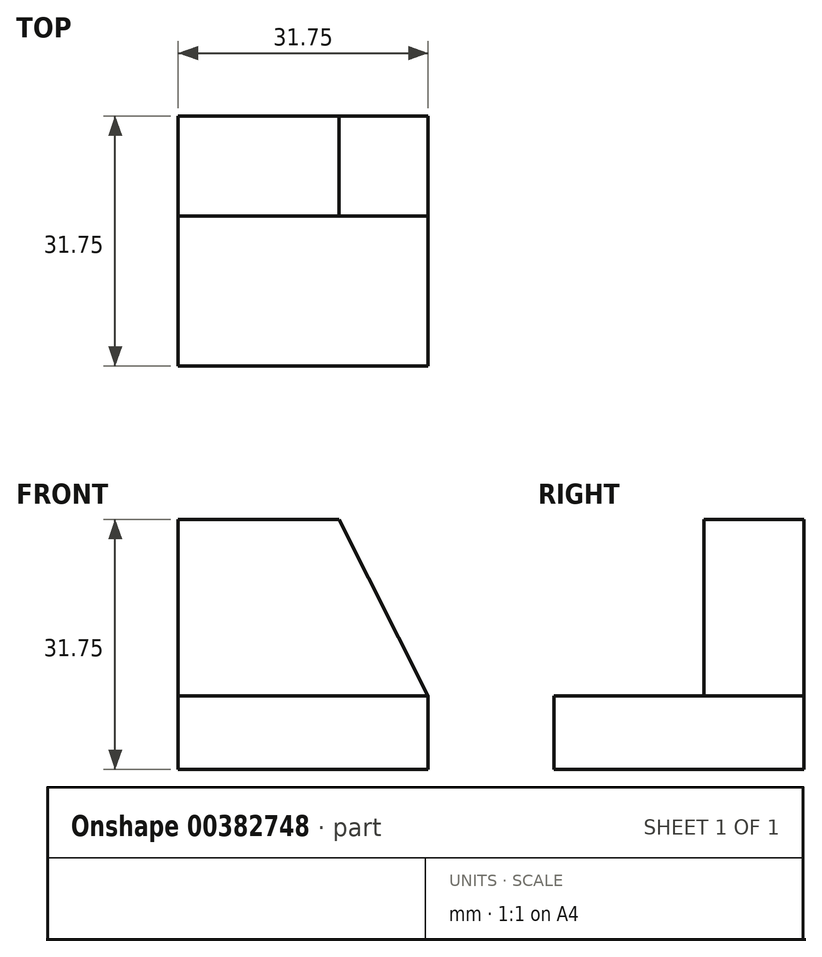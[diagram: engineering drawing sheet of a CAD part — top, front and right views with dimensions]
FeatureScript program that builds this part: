
annotation { "Feature Type Name" : "Feature", "Feature Type Description" : "" }
export const myFeature = defineFeature(function(context is Context, id is Id, definition is map)
    precondition{}
    {
        {
            var Q0;
            Q0=qCreatedBy(makeId("Right.planeOp"),FACE);
            var sketch = newSketch(context, id + "F0", { "sketchPlane" : qUnion([Q0])});
            skLineSegment(sketch, "E0", {"start": v(0, 0) * mm, "end": v(0, 9.33) * mm});
            skLineSegment(sketch, "E1", {"start": v(0, 9.33) * mm, "end": v(19.05, 9.33) * mm});
            skLineSegment(sketch, "E2", {"start": v(19.05, 9.33) * mm, "end": v(19.05, 31.75) * mm});
            skLineSegment(sketch, "E3", {"start": v(19.05, 31.75) * mm, "end": v(31.75, 31.75) * mm});
            skLineSegment(sketch, "E4", {"start": v(31.75, 31.75) * mm, "end": v(31.75, 0) * mm});
            skLineSegment(sketch, "E5", {"start": v(31.75, 0) * mm, "end": v(0, 0) * mm});
            skSolve(sketch);
        }
        {
            var Q0;
            Q0=makeQuery(id+"F0.imprint","IMPRINT",FACE,{"disambiguationData":[TD([[makeQuery(id+"F0.imprint","IMPRINT",EDGE,{"derivedFrom":sQuery(id+"F0.wireOp",EDGE,"E0")}),-1.0]])]});
            extrude(context, id + "F1", {"entities" : qUnion([Q0]), "depth" : 31.75 * mm});
        }
        {
            var Q0;
            Q0=makeQuery(id+"F1.opExtrude","SWEPT_FACE",FACE,{"disambiguationData":[OSD([sQuery(id+"F0.wireOp",EDGE,"E2")])]});
            var sketch = newSketch(context, id + "F2", { "sketchPlane" : qUnion([Q0])});
            skLineSegment(sketch, "E6", {"start": v(20.43, 31.75) * mm, "end": v(31.75, 9.33) * mm});
            skSolve(sketch);
        }
        {
            var Q0;
            {var subQ0=sQuery(id+"F2.wireOp",EDGE,"E6");Q0=makeQuery(id+"F2.imprint","IMPRINT",FACE,{"disambiguationData":[TD([[makeQuery(id+"F2.imprint","IMPRINT",EDGE,{"derivedFrom":subQ0}),1.0]])]});}
            extrude(context, id + "F3", {"entities" : qUnion([Q0]), "operationType" : NewBodyOperationType.REMOVE, "oppositeDirection" : true, "depth" : 25.4 * mm});
        }
    });
